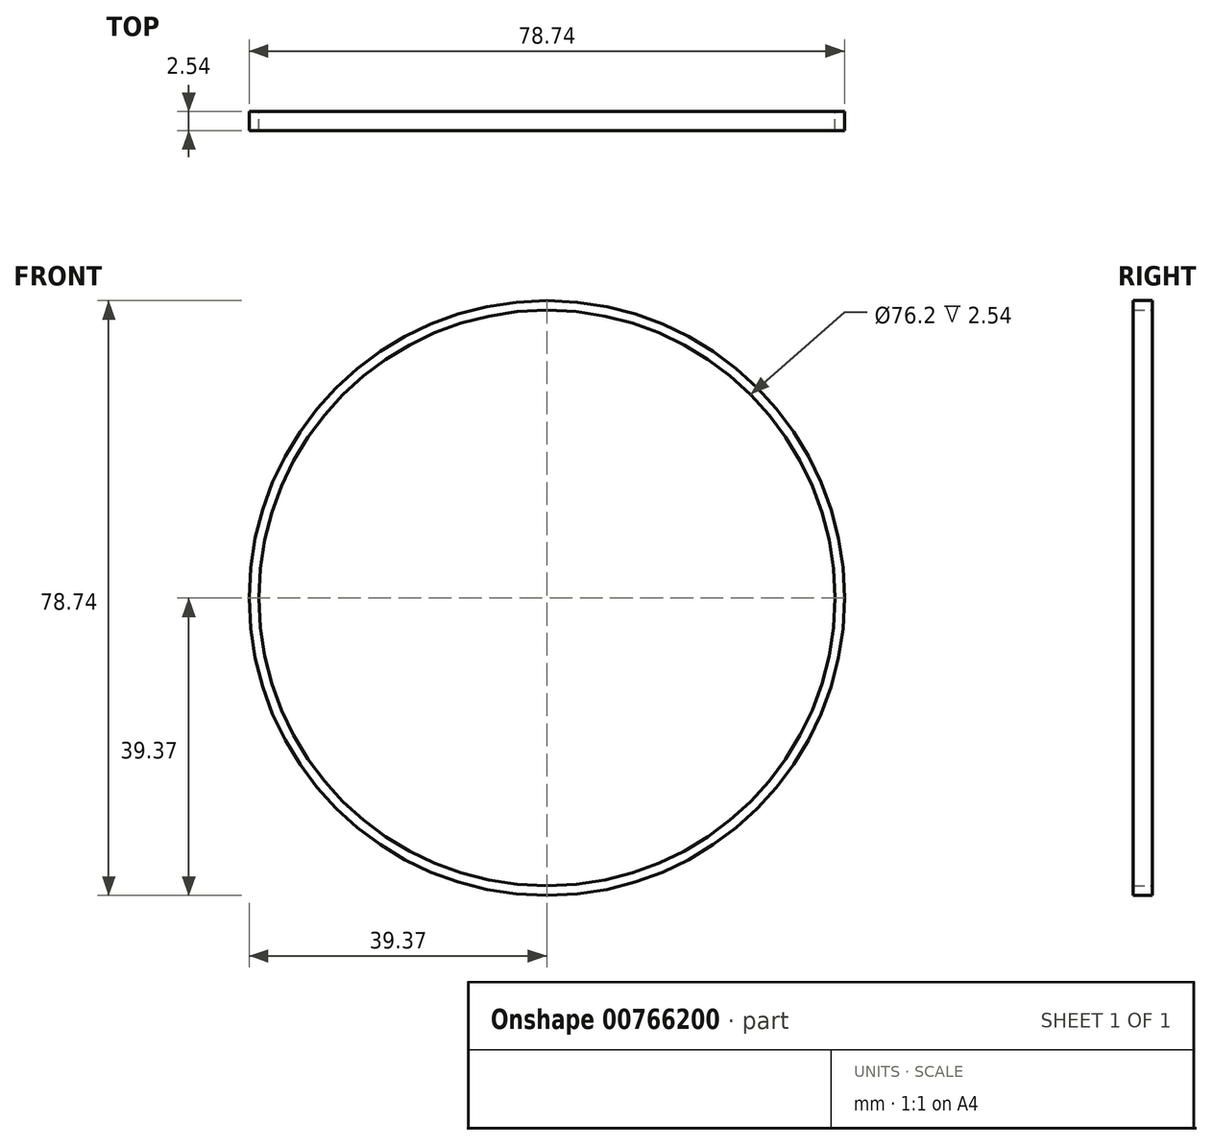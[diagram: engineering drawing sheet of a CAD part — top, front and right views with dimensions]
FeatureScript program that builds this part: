
annotation { "Feature Type Name" : "Feature", "Feature Type Description" : "" }
export const myFeature = defineFeature(function(context is Context, id is Id, definition is map)
    precondition{}
    {
        {
            var Q0;
            Q0=qCreatedBy(makeId("Front.planeOp"),FACE);
            var sketch = newSketch(context, id + "F0", { "sketchPlane" : qUnion([Q0])});
            skCircle(sketch, "E0", {"center": v(0, 0) * mm, "radius": 39.37 * mm});
            skCircle(sketch, "E1", {"center": v(0, 0) * mm, "radius": 38.1 * mm});
            skLineSegment(sketch, "E2", {"start": v(-39.37, 0) * mm, "end": v(-39.37, -52.27) * mm});
            skLineSegment(sketch, "E3", {"start": v(37.73, -12.93) * mm, "end": v(27.6, -72.07) * mm});
            skSolve(sketch);
        }
        {
            var Q0;
            Q0=makeQuery(id+"F0.imprint","IMPRINT",FACE,{"disambiguationData":[TD([[makeQuery(id+"F0.imprint","IMPRINT",EDGE,{"derivedFrom":sQuery(id+"F0.wireOp",EDGE,"E1")}),-1.0]])]});
            extrude(context, id + "F1", {"entities" : qUnion([Q0]), "depth" : 2.54 * mm, "offsetDistance" : 25.4 * mm});
        }
    });
